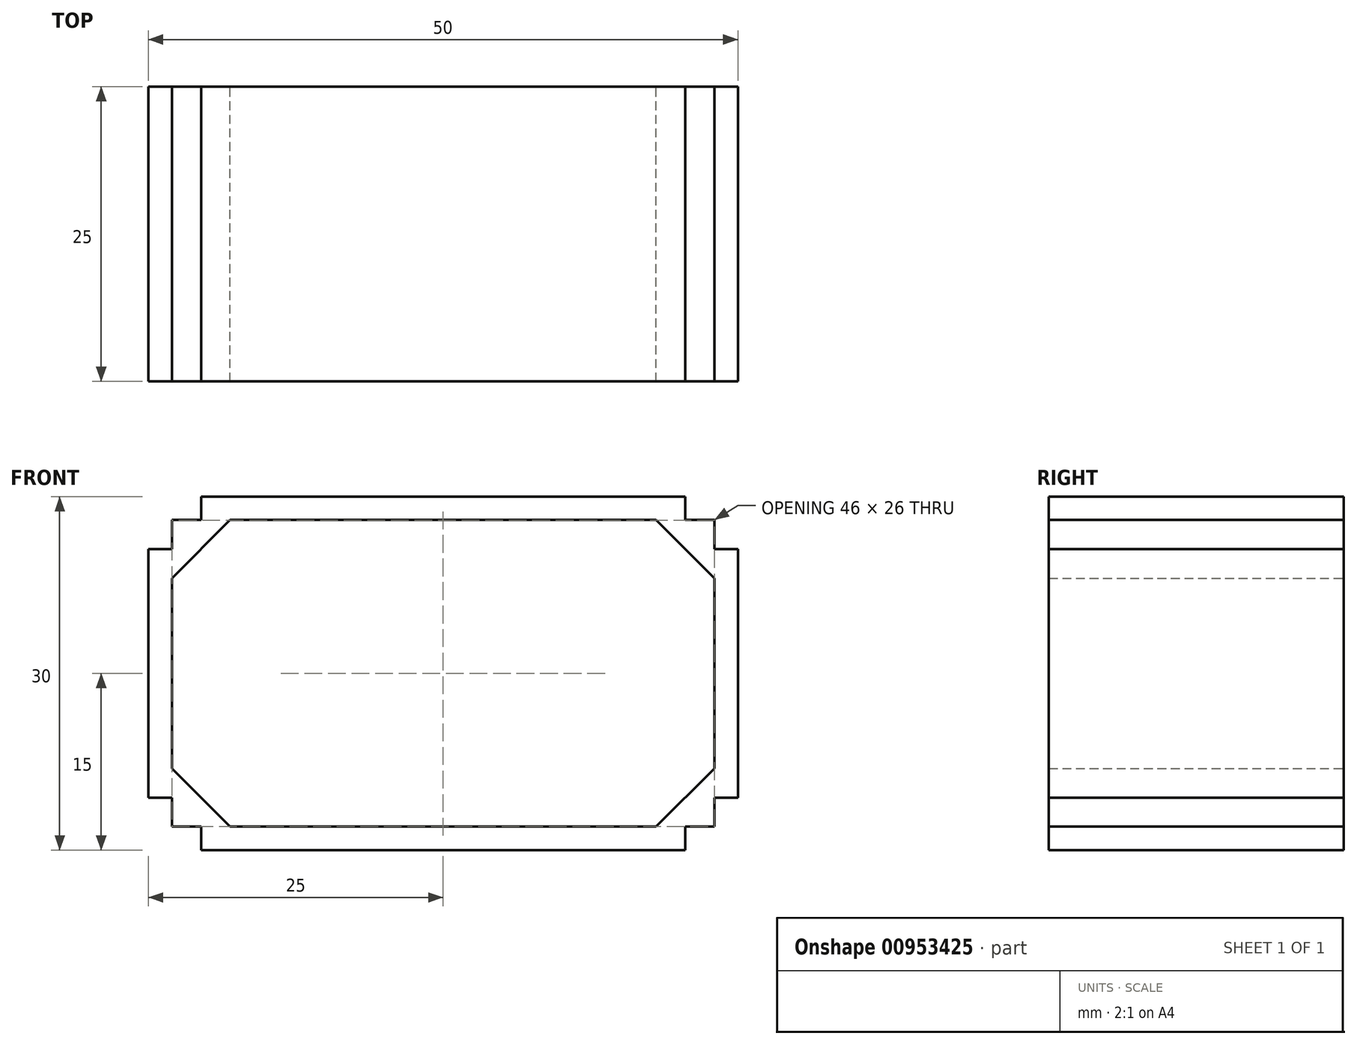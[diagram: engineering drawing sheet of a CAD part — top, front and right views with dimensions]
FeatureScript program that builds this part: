
annotation { "Feature Type Name" : "Feature", "Feature Type Description" : "" }
export const myFeature = defineFeature(function(context is Context, id is Id, definition is map)
    precondition{}
    {
        {
            var Q0;
            Q0=qCreatedBy(makeId("Front.planeOp"),FACE);
            var sketch = newSketch(context, id + "F0", { "sketchPlane" : qUnion([Q0])});
            skLineSegment(sketch, "E0.bottom", {"start": v(4.47, 0) * mm, "end": v(45.53, 0) * mm});
            skLineSegment(sketch, "E0.top", {"start": v(4.47, 30) * mm, "end": v(45.53, 30) * mm});
            skLineSegment(sketch, "E0.left", {"start": v(0, 4.47) * mm, "end": v(0, 25.53) * mm});
            skLineSegment(sketch, "E0.right", {"start": v(50, 4.47) * mm, "end": v(50, 25.53) * mm});
            skLineSegment(sketch, "E1.bottom", {"start": v(6.94, 2) * mm, "end": v(43.06, 2) * mm});
            skLineSegment(sketch, "E1.top", {"start": v(6.94, 28) * mm, "end": v(43.06, 28) * mm});
            skLineSegment(sketch, "E1.left", {"start": v(2, 6.94) * mm, "end": v(2, 23.06) * mm});
            skLineSegment(sketch, "E1.right", {"start": v(48, 6.94) * mm, "end": v(48, 23.06) * mm});
            skLineSegment(sketch, "E2", {"start": v(2, 23.06) * mm, "end": v(6.94, 28) * mm});
            skLineSegment(sketch, "E3", {"start": v(43.06, 28) * mm, "end": v(48, 23.06) * mm});
            skLineSegment(sketch, "E4", {"start": v(2, 6.94) * mm, "end": v(6.94, 2) * mm});
            skLineSegment(sketch, "E5", {"start": v(43.06, 2) * mm, "end": v(48, 6.94) * mm});
            skLineSegment(sketch, "E6", {"start": v(43.06, 28) * mm, "end": v(48, 28) * mm});
            skLineSegment(sketch, "E7", {"start": v(48, 28) * mm, "end": v(48, 23.06) * mm});
            skLineSegment(sketch, "E8", {"start": v(48, 6.94) * mm, "end": v(48, 2) * mm});
            skLineSegment(sketch, "E9", {"start": v(48, 2) * mm, "end": v(43.06, 2) * mm});
            skLineSegment(sketch, "E10", {"start": v(2, 6.94) * mm, "end": v(2, 2) * mm});
            skLineSegment(sketch, "E11", {"start": v(2, 2) * mm, "end": v(6.94, 2) * mm});
            skLineSegment(sketch, "E12", {"start": v(2, 23.06) * mm, "end": v(2, 28) * mm});
            skLineSegment(sketch, "E13", {"start": v(2, 28) * mm, "end": v(6.94, 28) * mm});
            skPoint(sketch, "E14", {"position": v(45.53, 28) * mm});
            skPoint(sketch, "E15", {"position": v(48, 25.53) * mm});
            skPoint(sketch, "E16", {"position": v(48, 4.47) * mm});
            skPoint(sketch, "E17", {"position": v(45.53, 2) * mm});
            skPoint(sketch, "E18", {"position": v(4.47, 2) * mm});
            skPoint(sketch, "E19", {"position": v(2, 4.47) * mm});
            skPoint(sketch, "E20", {"position": v(2, 25.53) * mm});
            skPoint(sketch, "E21", {"position": v(4.47, 28) * mm});
            skLineSegment(sketch, "E22", {"start": v(45.53, 28) * mm, "end": v(45.53, 30) * mm});
            skLineSegment(sketch, "E23", {"start": v(48, 25.53) * mm, "end": v(50, 25.53) * mm});
            skLineSegment(sketch, "E24", {"start": v(48, 4.47) * mm, "end": v(50, 4.47) * mm});
            skLineSegment(sketch, "E25", {"start": v(45.53, 2) * mm, "end": v(45.53, 0) * mm});
            skLineSegment(sketch, "E26", {"start": v(4.47, 2) * mm, "end": v(4.47, 0) * mm});
            skLineSegment(sketch, "E27", {"start": v(2, 4.47) * mm, "end": v(0, 4.47) * mm});
            skLineSegment(sketch, "E28", {"start": v(2, 25.53) * mm, "end": v(0, 25.53) * mm});
            skLineSegment(sketch, "E29", {"start": v(4.47, 28) * mm, "end": v(4.47, 30) * mm});
            skSolve(sketch);
        }
        {
            var Q0;
            Q0 = qSketchRegion(id + "F0", true);
            extrude(context, id + "F1", {"entities" : qUnion([Q0]), "depth" : 25 * mm, "offsetDistance" : 25 * mm});
        }
    });
